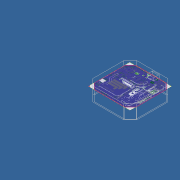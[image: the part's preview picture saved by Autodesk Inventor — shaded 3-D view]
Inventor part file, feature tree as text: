
AUTODESK INVENTOR PART (.ipt)
format: ipt  version: unknown  size: 1,211,392 bytes
history: native  units: mm
features: sketch x8, extrude x7, other x1
ambient origin geometry x8: Origin, YZ Plane, XZ Plane, XY Plane, X Axis, Y Axis, Z Axis, Center Point
bodies: Solido1 (feature_tree)
feature tree (16):
  extrude  "Estrusione1"  Depth=15.0mm TaperAngle=0.0deg
  extrude  "Estrusione6"  Depth=59.0mm
  sketch  "Schizzo8"
  extrude  "Estrusione7"  Depth=59.0mm
  extrude  "Estrusione8"  Depth=8.0mm
  extrude  "Estrusione9"  Depth=8.0mm
  extrude  "Estrusione10"  Depth=59.0mm
  extrude  "Estrusione11"  Depth=8.0mm
  sketch  "Schizzo1"
  sketch  "Schizzo7"
  other  "Immagine2"
  sketch  "Schizzo9"
  sketch  "Schizzo10"
  sketch  "Schizzo11"
  sketch  "Schizzo12"
  sketch  "Schizzo13"
